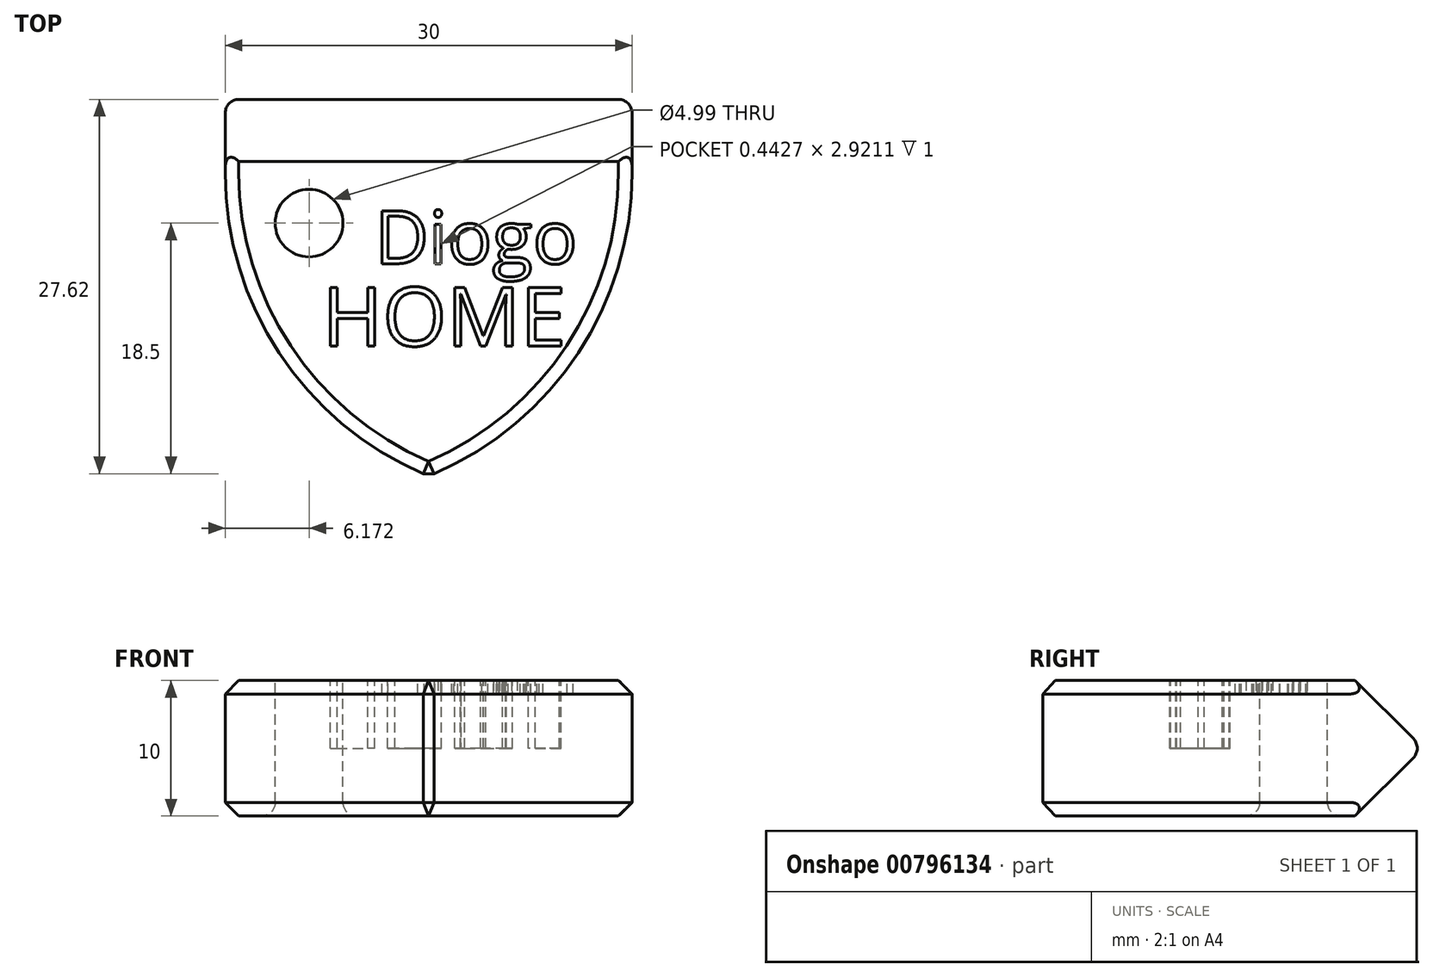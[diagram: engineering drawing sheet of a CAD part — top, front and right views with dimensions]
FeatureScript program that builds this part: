
annotation { "Feature Type Name" : "Feature", "Feature Type Description" : "" }
export const myFeature = defineFeature(function(context is Context, id is Id, definition is map)
    precondition{}
    {
        {
            var Q0;
            Q0=qCreatedBy(makeId("Top.planeOp"),FACE);
            var sketch = newSketch(context, id + "F0", { "sketchPlane" : qUnion([Q0])});
            skLineSegment(sketch, "E0.bottom", {"start": v(-16.25, 9.54) * mm, "end": v(13.75, 9.54) * mm});
            skLineSegment(sketch, "E0.top", {"start": v(-16.25, -20.46) * mm, "end": v(13.75, -20.46) * mm});
            skLineSegment(sketch, "E0.left", {"start": v(-16.25, 9.54) * mm, "end": v(-16.25, -20.46) * mm});
            skLineSegment(sketch, "E0.right", {"start": v(13.75, 9.54) * mm, "end": v(13.75, -20.46) * mm});
            skSolve(sketch);
        }
        {
            var Q0;
            Q0 = qSketchRegion(id + "F0", true);
            extrude(context, id + "F1", {"entities" : qUnion([Q0]), "depth" : 10 * mm, "offsetDistance" : 25 * mm});
        }
        {
            var Q0;
            Q0=makeQuery(id+"F1.opExtrude","SWEPT_EDGE",EDGE,{"disambiguationData":[OSD([sQuery(id+"F0.wireOp",EDGE,"E0.top"),sQuery(id+"F0.wireOp",EDGE,"E0.left")])]});
            var Q1;
            Q1=makeQuery(id+"F1.opExtrude","SWEPT_EDGE",EDGE,{"disambiguationData":[OSD([sQuery(id+"F0.wireOp",EDGE,"E0.top"),sQuery(id+"F0.wireOp",EDGE,"E0.right")])]});
            fillet(context, id + "F2", {"entities" : qUnion([Q0, Q1]), "radius" : 24.14 * mm, "tangentPropagation" : true, "allowEdgeOverflow" : false});
        }
        {
            var Q0;
            Q0=makeQuery(id+"F1.opExtrude","CAP_EDGE",EDGE,{"disambiguationData":[OSD([sQuery(id+"F0.wireOp",EDGE,"E0.bottom")])],"isStart":false});
            chamfer(context, id + "F3", {"entities" : qUnion([Q0]), "width" : 5 * mm, "tangentPropagation" : true});
        }
        {
            var Q0;
            Q0=makeQuery(id+"F1.opExtrude","CAP_FACE",FACE,{"disambiguationData":[OSD([sQuery(id+"F0.wireOp",EDGE,"E0.bottom"),sQuery(id+"F0.wireOp",EDGE,"E0.top"),sQuery(id+"F0.wireOp",EDGE,"E0.left"),sQuery(id+"F0.wireOp",EDGE,"E0.right")])],"isStart":false});
            var sketch = newSketch(context, id + "F4", { "sketchPlane" : qUnion([Q0])});
            skText(sketch, "E1", { "text": "HOME", "fontName": "OpenSans-Regular.ttf"});
            const initialGuessF4  = {"E1": [-0.0091, -0.00907, 1, 0, 0.00435]};
            skSetInitialGuess(sketch, initialGuessF4);
            skSolve(sketch);
        }
        {
            var Q0;
            Q0 = qSketchRegion(id + "F4", true);
            extrude(context, id + "F5", {"entities" : qUnion([Q0]), "operationType" : NewBodyOperationType.REMOVE, "oppositeDirection" : true, "depth" : 5 * mm, "offsetDistance" : 25 * mm});
        }
        {
            var Q0;
            Q0=makeQuery(id+"F1.opExtrude","CAP_EDGE",EDGE,{"disambiguationData":[OSD([sQuery(id+"F0.wireOp",EDGE,"E0.bottom")])],"isStart":true});
            chamfer(context, id + "F6", {"entities" : qUnion([Q0]), "width" : 5 * mm, "tangentPropagation" : true});
        }
        {
            var Q0;
            Q0=makeQuery(id+"F6.opChamfer","BLEND_EDGE",EDGE,{"blendedFrom":[makeQuery(id+"F1.opExtrude","CAP_EDGE",EDGE,{"disambiguationData":[OSD([sQuery(id+"F0.wireOp",EDGE,"E0.bottom")])],"isStart":true}),makeQuery(id+"F1.opExtrude","SWEPT_FACE",FACE,{"disambiguationData":[OSD([sQuery(id+"F0.wireOp",EDGE,"E0.left")])]})],"blendedInto":[makeQuery(id+"F1.opExtrude","SWEPT_FACE",FACE,{"disambiguationData":[OSD([sQuery(id+"F0.wireOp",EDGE,"E0.left")])]})]});
            var Q1;
            Q1=makeQuery(id+"F3.opChamfer","BLEND_EDGE",EDGE,{"blendedFrom":[makeQuery(id+"F1.opExtrude","CAP_EDGE",EDGE,{"disambiguationData":[OSD([sQuery(id+"F0.wireOp",EDGE,"E0.bottom")])],"isStart":false}),makeQuery(id+"F1.opExtrude","SWEPT_FACE",FACE,{"disambiguationData":[OSD([sQuery(id+"F0.wireOp",EDGE,"E0.left")])]})],"blendedInto":[makeQuery(id+"F1.opExtrude","SWEPT_FACE",FACE,{"disambiguationData":[OSD([sQuery(id+"F0.wireOp",EDGE,"E0.left")])]})]});
            var Q2;
            {var subQ0=sQuery(id+"F0.wireOp",EDGE,"E0.bottom");Q2=makeQuery(id+"F6.opChamfer","BLEND_EDGE",EDGE,{"blendedFrom":[makeQuery(id+"F1.opExtrude","CAP_EDGE",EDGE,{"disambiguationData":[OSD([subQ0])],"isStart":true}),makeQuery(id+"F3.opChamfer","BLEND_FACE",FACE,{"disambiguationData":[OSD([subQ0])]})],"blendedInto":[makeQuery(id+"F3.opChamfer","BLEND_FACE",FACE,{"disambiguationData":[OSD([subQ0])]})]});}
            var Q3;
            Q3=makeQuery(id+"F6.opChamfer","BLEND_EDGE",EDGE,{"blendedFrom":[makeQuery(id+"F1.opExtrude","CAP_EDGE",EDGE,{"disambiguationData":[OSD([sQuery(id+"F0.wireOp",EDGE,"E0.bottom")])],"isStart":true}),makeQuery(id+"F1.opExtrude","SWEPT_FACE",FACE,{"disambiguationData":[OSD([sQuery(id+"F0.wireOp",EDGE,"E0.right")])]})],"blendedInto":[makeQuery(id+"F1.opExtrude","SWEPT_FACE",FACE,{"disambiguationData":[OSD([sQuery(id+"F0.wireOp",EDGE,"E0.right")])]})]});
            var Q4;
            Q4=makeQuery(id+"F3.opChamfer","BLEND_EDGE",EDGE,{"blendedFrom":[makeQuery(id+"F1.opExtrude","CAP_EDGE",EDGE,{"disambiguationData":[OSD([sQuery(id+"F0.wireOp",EDGE,"E0.bottom")])],"isStart":false}),makeQuery(id+"F1.opExtrude","SWEPT_FACE",FACE,{"disambiguationData":[OSD([sQuery(id+"F0.wireOp",EDGE,"E0.right")])]})],"blendedInto":[makeQuery(id+"F1.opExtrude","SWEPT_FACE",FACE,{"disambiguationData":[OSD([sQuery(id+"F0.wireOp",EDGE,"E0.right")])]})]});
            fillet(context, id + "F7", {"entities" : qUnion([Q0, Q1, Q2, Q3, Q4]), "radius" : 1 * mm, "tangentPropagation" : true, "allowEdgeOverflow" : false});
        }
        {
            var Q0;
            {var subQ0=sQuery(id+"F0.wireOp",EDGE,"E0.left");var subQ1=sQuery(id+"F0.wireOp",EDGE,"E0.top");Q0=makeQuery(id+"F2.opFillet","BLEND_EDGE",EDGE,{"blendedFrom":[makeQuery(id+"F1.opExtrude","SWEPT_EDGE",EDGE,{"disambiguationData":[OSD([subQ1,subQ0])]}),makeQuery(id+"F1.opExtrude","CAP_FACE",FACE,{"disambiguationData":[OSD([sQuery(id+"F0.wireOp",EDGE,"E0.bottom"),subQ1,subQ0,sQuery(id+"F0.wireOp",EDGE,"E0.right")])],"isStart":false})],"blendedInto":[makeQuery(id+"F1.opExtrude","CAP_FACE",FACE,{"disambiguationData":[OSD([sQuery(id+"F0.wireOp",EDGE,"E0.bottom"),subQ1,subQ0,sQuery(id+"F0.wireOp",EDGE,"E0.right")])],"isStart":false})]});}
            var Q1;
            {var subQ0=sQuery(id+"F0.wireOp",EDGE,"E0.right");var subQ1=sQuery(id+"F0.wireOp",EDGE,"E0.top");Q1=makeQuery(id+"F2.opFillet","BLEND_EDGE",EDGE,{"blendedFrom":[makeQuery(id+"F1.opExtrude","SWEPT_EDGE",EDGE,{"disambiguationData":[OSD([subQ1,subQ0])]}),makeQuery(id+"F1.opExtrude","CAP_FACE",FACE,{"disambiguationData":[OSD([sQuery(id+"F0.wireOp",EDGE,"E0.bottom"),subQ1,sQuery(id+"F0.wireOp",EDGE,"E0.left"),subQ0])],"isStart":false})],"blendedInto":[makeQuery(id+"F1.opExtrude","CAP_FACE",FACE,{"disambiguationData":[OSD([sQuery(id+"F0.wireOp",EDGE,"E0.bottom"),subQ1,sQuery(id+"F0.wireOp",EDGE,"E0.left"),subQ0])],"isStart":false})]});}
            var Q2;
            {var subQ0=sQuery(id+"F0.wireOp",EDGE,"E0.right");var subQ1=sQuery(id+"F0.wireOp",EDGE,"E0.top");Q2=makeQuery(id+"F2.opFillet","BLEND_EDGE",EDGE,{"blendedFrom":[makeQuery(id+"F1.opExtrude","SWEPT_EDGE",EDGE,{"disambiguationData":[OSD([subQ1,subQ0])]}),makeQuery(id+"F1.opExtrude","CAP_FACE",FACE,{"disambiguationData":[OSD([sQuery(id+"F0.wireOp",EDGE,"E0.bottom"),subQ1,sQuery(id+"F0.wireOp",EDGE,"E0.left"),subQ0])],"isStart":true})],"blendedInto":[makeQuery(id+"F1.opExtrude","CAP_FACE",FACE,{"disambiguationData":[OSD([sQuery(id+"F0.wireOp",EDGE,"E0.bottom"),subQ1,sQuery(id+"F0.wireOp",EDGE,"E0.left"),subQ0])],"isStart":true})]});}
            var Q3;
            {var subQ0=sQuery(id+"F0.wireOp",EDGE,"E0.left");var subQ1=sQuery(id+"F0.wireOp",EDGE,"E0.top");Q3=makeQuery(id+"F2.opFillet","BLEND_EDGE",EDGE,{"blendedFrom":[makeQuery(id+"F1.opExtrude","SWEPT_EDGE",EDGE,{"disambiguationData":[OSD([subQ1,subQ0])]}),makeQuery(id+"F1.opExtrude","CAP_FACE",FACE,{"disambiguationData":[OSD([sQuery(id+"F0.wireOp",EDGE,"E0.bottom"),subQ1,subQ0,sQuery(id+"F0.wireOp",EDGE,"E0.right")])],"isStart":true})],"blendedInto":[makeQuery(id+"F1.opExtrude","CAP_FACE",FACE,{"disambiguationData":[OSD([sQuery(id+"F0.wireOp",EDGE,"E0.bottom"),subQ1,subQ0,sQuery(id+"F0.wireOp",EDGE,"E0.right")])],"isStart":true})]});}
            var Q4;
            {var subQ0=sQuery(id+"F0.wireOp",EDGE,"E0.top");Q4=makeQuery(id+"F2.opFillet","BLEND_EDGE",EDGE,{"blendedFrom":[makeQuery(id+"F1.opExtrude","SWEPT_EDGE",EDGE,{"disambiguationData":[OSD([subQ0,sQuery(id+"F0.wireOp",EDGE,"E0.left")])]}),makeQuery(id+"F1.opExtrude","SWEPT_EDGE",EDGE,{"disambiguationData":[OSD([subQ0,sQuery(id+"F0.wireOp",EDGE,"E0.right")])]})],"blendedInto":[]});}
            chamfer(context, id + "F8", {"entities" : qUnion([Q0, Q1, Q2, Q3, Q4]), "width" : 1 * mm, "tangentPropagation" : true});
        }
        {
            var Q0;
            {var subQ0=sQuery(id+"F0.wireOp",EDGE,"E0.bottom");var subQ1=sQuery(id+"F0.wireOp",EDGE,"E0.right");var subQ2=sQuery(id+"F0.wireOp",EDGE,"E0.top");var subQ3=sQuery(id+"F0.wireOp",EDGE,"E0.left");Q0=makeQuery(id+"F5.boolean.opBoolean","SPLIT",FACE,{"disambiguationData":[TD([makeQuery(id+"F1.opExtrude","SWEPT_FACE",FACE,{"disambiguationData":[OSD([subQ3])]})])],"derivedFrom":makeQuery(id+"F1.opExtrude","CAP_FACE",FACE,{"disambiguationData":[OSD([subQ0,subQ2,subQ3,subQ1])],"isStart":false})});}
            var sketch = newSketch(context, id + "F9", { "sketchPlane" : qUnion([Q0])});
            skText(sketch, "E2", { "text": "Diogo", "fontName": "OpenSans-Regular.ttf"});
            const initialGuessF9  = {"E2": [-0.00523, -0.003, 1, 0, 0.00393]};
            skSetInitialGuess(sketch, initialGuessF9);
            skSolve(sketch);
        }
        {
            var Q0;
            Q0 = qSketchRegion(id + "F9", true);
            extrude(context, id + "F10", {"entities" : qUnion([Q0]), "operationType" : NewBodyOperationType.REMOVE, "oppositeDirection" : true, "depth" : 1 * mm, "offsetDistance" : 25 * mm});
        }
        {
            var Q0;
            {var subQ0=sQuery(id+"F0.wireOp",EDGE,"E0.right");var subQ1=sQuery(id+"F0.wireOp",EDGE,"E0.left");var subQ2=sQuery(id+"F0.wireOp",EDGE,"E0.top");var subQ3=sQuery(id+"F0.wireOp",EDGE,"E0.bottom");var subQ4=makeQuery(id+"F1.opExtrude","CAP_FACE",FACE,{"disambiguationData":[OSD([subQ3,subQ2,subQ1,subQ0])],"isStart":false});var subQ20=makeQuery(id+"F1.opExtrude","SWEPT_FACE",FACE,{"disambiguationData":[OSD([subQ1])]});var subQ34=makeQuery(id+"F3.opChamfer","BLEND_FACE",FACE,{"disambiguationData":[OSD([subQ3])]});Q0=makeQuery(id+"F10.boolean.opBoolean","SPLIT",FACE,{"disambiguationData":[TD([subQ34])],"derivedFrom":makeQuery(id+"F5.boolean.opBoolean","SPLIT",FACE,{"disambiguationData":[TD([subQ20])],"derivedFrom":subQ4})});}
            var sketch = newSketch(context, id + "F11", { "sketchPlane" : qUnion([Q0])});
            skCircle(sketch, "E3", {"center": v(-10.08, 0) * mm, "radius": 2.5 * mm});
            skSolve(sketch);
        }
        {
            var Q0;
            Q0 = qSketchRegion(id + "F11", true);
            extrude(context, id + "F12", {"entities" : qUnion([Q0]), "operationType" : NewBodyOperationType.REMOVE, "oppositeDirection" : true, "depth" : 25 * mm, "offsetDistance" : 25 * mm});
        }
        {
            var Q0;
            Q0=makeQuery(id+"F12.boolean.opBoolean","COPY",EDGE,{"derivedFrom":makeQuery(id+"F12.opExtrude","CAP_EDGE",EDGE,{"disambiguationData":[OSD([sQuery(id+"F11.wireOp",EDGE,"E3")])],"isStart":true})});
            var Q1;
            Q1=makeQuery(id+"F12.boolean.opBoolean","INTERSECT",EDGE,{"derivedFrom":[makeQuery(id+"F1.opExtrude","CAP_FACE",FACE,{"disambiguationData":[OSD([sQuery(id+"F0.wireOp",EDGE,"E0.bottom"),sQuery(id+"F0.wireOp",EDGE,"E0.top"),sQuery(id+"F0.wireOp",EDGE,"E0.left"),sQuery(id+"F0.wireOp",EDGE,"E0.right")])],"isStart":true}),makeQuery(id+"F12.opExtrude","SWEPT_FACE",FACE,{"disambiguationData":[OSD([sQuery(id+"F11.wireOp",EDGE,"E3")])]})]});
            fillet(context, id + "F13", {"entities" : qUnion([Q0, Q1]), "radius" : 1 * mm, "tangentPropagation" : true, "allowEdgeOverflow" : false});
        }
    });
